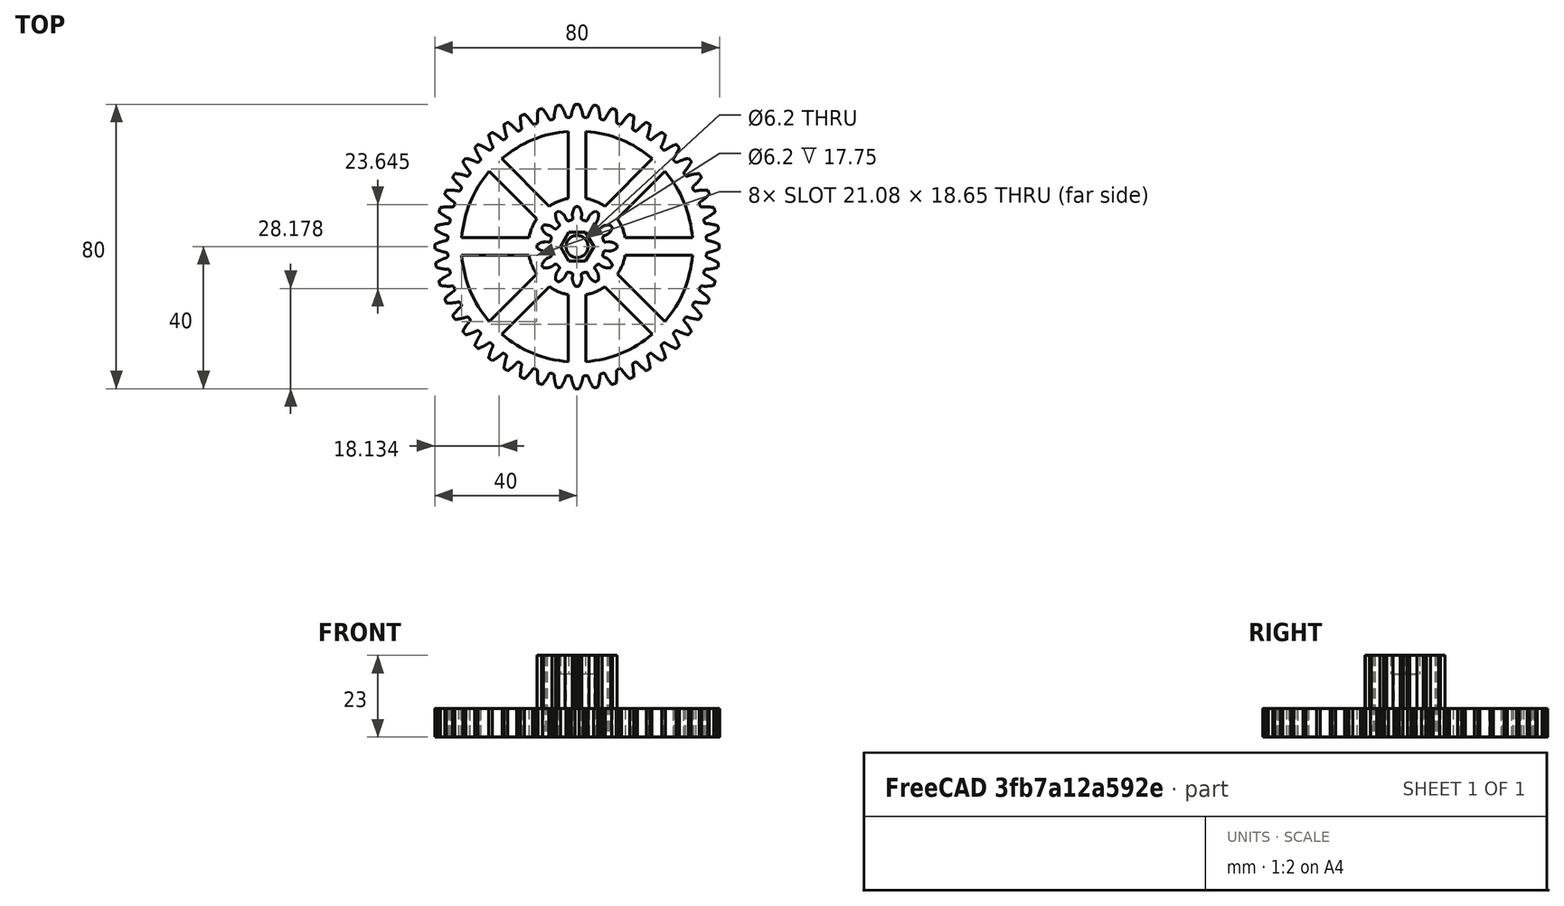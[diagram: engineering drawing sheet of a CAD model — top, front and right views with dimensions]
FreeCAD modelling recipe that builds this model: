
FCSTD DOCUMENT  (FreeCAD 0.20R29177 (Git))
Label: TOP_-_Part_5C_-_DoubleGear48t
License: All rights reserved
LicenseURL: http://en.wikipedia.org/wiki/All_rights_reserved
objects: Part::Part2DObjectPython×3, Part::Extrusion×3, Part::Cut×3, Mesh::Feature×1, Part::Cylinder×1, Sketcher::SketchObject×1, PartDesign::FeatureBase×1, PartDesign::Pocket×1, PartDesign::PolarPattern×1, PartDesign::Body×1, Part::RegularPolygon×1
note: 17 computed .brp shape members not serialized (recipe doc carries the construction recipe); baked Part::Feature solids carry a one-line shape summary decoded from their .brp

FEATURE [Mesh::Feature] TOP___Part_5C___DoubleGear  label="TOP_-_Part_5C_-_DoubleGear"
  Placement = pos=(88.45,-90.1,-31) rot=(0,0,1;0rad)
FEATURE [Part::Part2DObjectPython] InvoluteGear  label="InvoluteGear12t"  # Draft 2D object (typed FeaturePython)
  ExternalGear = true
  HighPrecision = false
  Modules = 1.6
  NumberOfTeeth = 12
  PressureAngle = 20
FEATURE [Part::Part2DObjectPython] InvoluteGear001  label="InvoluteGear30t"  # Draft 2D object (typed FeaturePython)
  ExternalGear = true
  HighPrecision = false
  Modules = 1.6
  NumberOfTeeth = 30
  Placement = pos=(0,0,0) rot=(0,0,1;0.314159rad)
  PressureAngle = 20
FEATURE [Part::Part2DObjectPython] InvoluteGear002  label="InvoluteGear48t"  # Draft 2D object (typed FeaturePython)
  ExternalGear = true
  HighPrecision = false
  Modules = 1.6
  NumberOfTeeth = 48
  Placement = pos=(0,0,-15) rot=(0,0,1;0rad)
  PressureAngle = 20
FEATURE [Part::Extrusion] Extrude001
  Base = -> InvoluteGear002
  Dir = (0,0,1)
  DirMode = 2
  FaceMakerClass = Part::FaceMakerBullseye
  LengthFwd = 8
  LengthRev = 0
  Reversed = true
  Solid = true
  Symmetric = false
FEATURE [Part::Extrusion] Extrude
  Base = -> InvoluteGear
  Dir = (0,0,1)
  DirMode = 2
  FaceMakerClass = Part::FaceMakerBullseye
  LengthFwd = 23
  LengthRev = 0
  Reversed = true
  Solid = true
  Symmetric = false
FEATURE [Part::Cylinder] Cylinder
  Angle = 360
  AttacherType = Attacher::AttachEngine3D
  FirstAngle = 0
  Height = 24
  Placement = pos=(0,0,-23.5) rot=(0,0,1;0rad)
  Radius = 3.1
  SecondAngle = 0
FEATURE [Part::Cut] Cut
  Base = -> Extrude
  Tool = -> Cylinder
FEATURE [Part::Cut] Cut001
  Base = -> Extrude001
  Tool = -> Cylinder
FEATURE [Sketcher::SketchObject] Sketch001
  FullyConstrained = false
  MapMode = 5
  Support = -> [XY_Plane]
  sketch-geometry (4):
    g0: ArcOfCircle CenterX=0 CenterY=-4.27746e-07 CenterZ=0 NormalX=0 NormalY=0 NormalZ=1 AngleXU=0 Radius=32.5 StartAngle=1.6478 EndAngle=2.2792
    g1: ArcOfCircle CenterX=0 CenterY=0 CenterZ=0 NormalX=0 NormalY=0 NormalZ=1 AngleXU=0 Radius=13.75 StartAngle=1.75363 EndAngle=2.17336
    g2: LineSegment StartX=-2.5 StartY=32.4037 StartZ=0 EndX=-2.5 EndY=13.5208 EndZ=0
    g3: LineSegment StartX=-7.79289 StartY=11.3284 StartZ=0 EndX=-21.1451 EndY=24.6806 EndZ=0
  constraints (8):
    c: DistanceX(g0,g-1) = 2.5
    c: Diameter(g0) = 65
    c: Diameter(g1) = 27.5
    c: Coincident(g2,g0)
    c: Coincident(g2,g1)
    c: Vertical(g2)
    c: Coincident(g3,g1)
    c: Coincident(g3,g0)
FEATURE [PartDesign::FeatureBase] BaseFeature
  BaseFeature = -> Cut001
FEATURE [PartDesign::Pocket] Pocket
  BaseFeature = -> BaseFeature
  Direction = (0,0,-1)
  Length = 22
  Length2 = 5
  Profile = -> Sketch001
  ReferenceAxis = -> Sketch001 [N_Axis]
  Type = 1
FEATURE [PartDesign::PolarPattern] PolarPattern
  Angle = 360
  Axis = -> Sketch001 [N_Axis]
  BaseFeature = -> Pocket
  Occurrences = 8
  Originals = -> [Pocket]
FEATURE [PartDesign::Body] Body
  BaseFeature = -> Cut001
  Group = -> [BaseFeature,Extrude001,Extrude,Sketch001,Pocket,PolarPattern]
  Origin = -> Origin
  Tip = -> PolarPattern
FEATURE [Part::RegularPolygon] RegularPolygon001  label="Regular polygon001"
  AttacherType = Attacher::AttachEngine3D
  Circumradius = 4.7
  Polygon = 6
FEATURE [Part::Extrusion] Extrude002
  Base = -> RegularPolygon001
  Dir = (0,0,1)
  DirMode = 2
  FaceMakerClass = Part::FaceMakerBullseye
  LengthFwd = 5.25
  LengthRev = 0
  Reversed = true
  Solid = true
  Symmetric = false
FEATURE [Part::Cut] Cut002
  Base = -> Cut
  Tool = -> Extrude002
